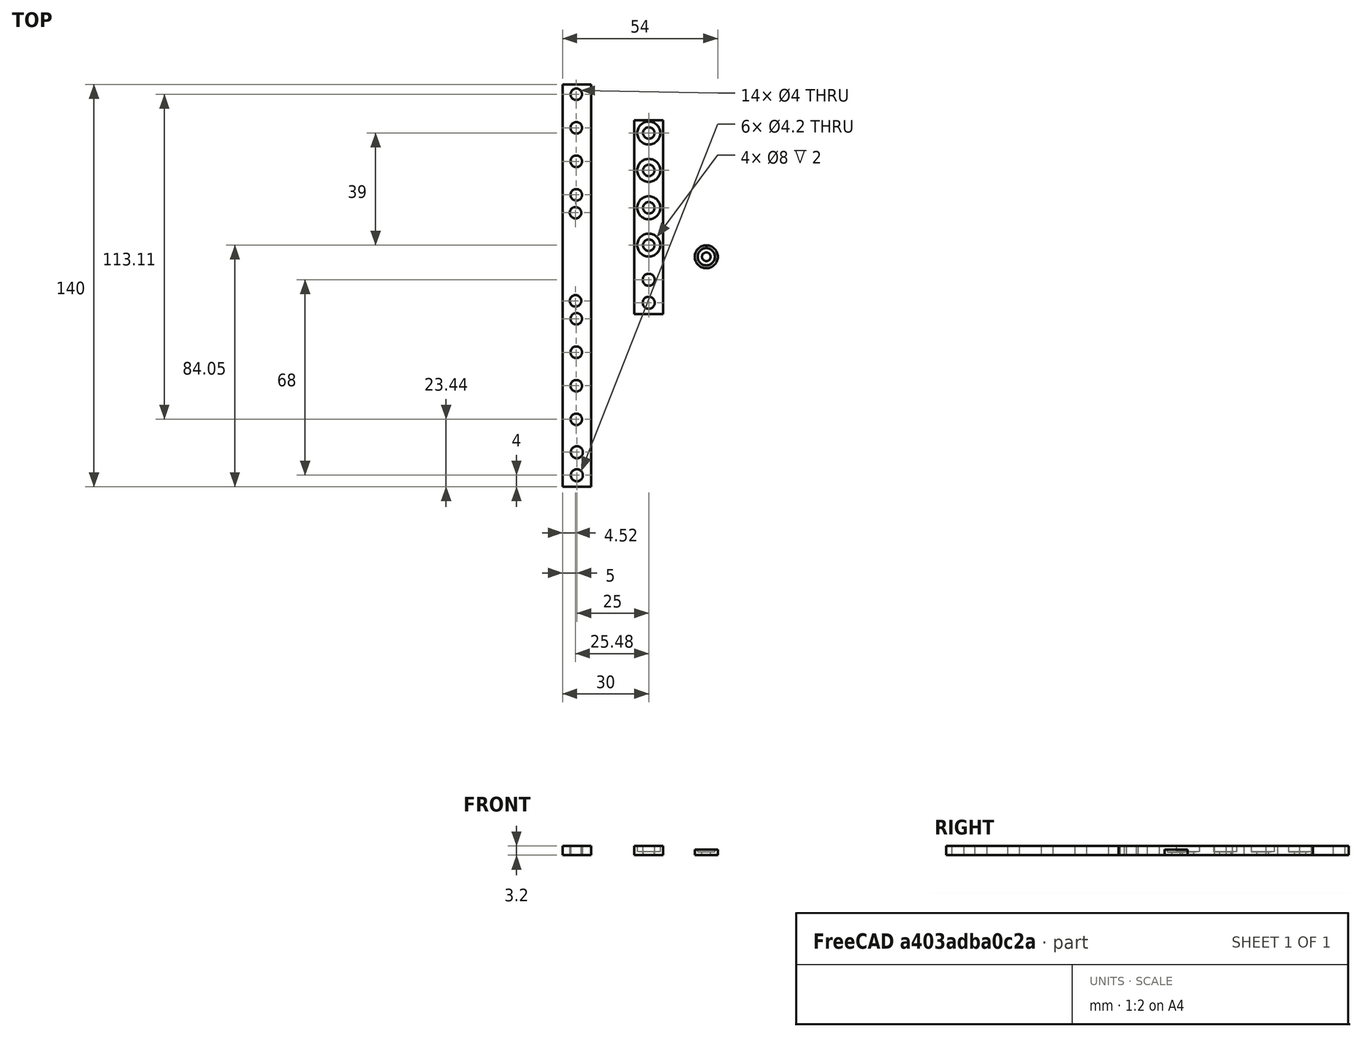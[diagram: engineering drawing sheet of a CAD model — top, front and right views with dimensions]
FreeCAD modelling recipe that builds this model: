
FCSTD DOCUMENT  (FreeCAD 0.19R24291 (Git))
Label: busbars
License: All rights reserved
LicenseURL: http://en.wikipedia.org/wiki/All_rights_reserved
objects: TechDraw::DrawViewDimension×44, Part::Cylinder×18, PartDesign::Line×18, Part::Fuse×7, TechDraw::DrawProjGroupItem×6, Part::Box×5, Part::Cut×5, Part::MultiFuse×4, Sketcher::SketchObject×3, PartDesign::CoordinateSystem×3, PartDesign::Hole×3, PartDesign::Body×3, Part::Part2DObjectPython×2, PartDesign::Pad×2, TechDraw::DrawProjGroup×2, App::DocumentObjectGroup×2, TechDraw::DrawViewPart×2, Part::FeaturePython×2, Part::Mirroring×1, TechDraw::DrawSVGTemplate×1, +4 more types
note: 82 computed .brp shape members not serialized (recipe doc carries the construction recipe); baked Part::Feature solids carry a one-line shape summary decoded from their .brp

FEATURE [Part::Box] cube
  AttacherType = Attacher::AttachEngine3D
  Height = 3
  Length = 10
  Width = 60
FEATURE [Part::Cylinder] cylinder
  Angle = 360
  AttacherType = Attacher::AttachEngine3D
  Height = 5
  Placement = pos=(4.81,56.54,-1) rot=(0,0,1;0rad)
  Radius = 1.6
FEATURE [Part::Cylinder] cylinder001
  Angle = 360
  AttacherType = Attacher::AttachEngine3D
  Height = 5
  Placement = pos=(4.81,44.87,-1) rot=(0,0,1;0rad)
  Radius = 1.6
FEATURE [Part::Cylinder] cylinder002
  Angle = 360
  AttacherType = Attacher::AttachEngine3D
  Height = 5
  Placement = pos=(4.81,33.2,-1) rot=(0,0,1;0rad)
  Radius = 1.6
FEATURE [Part::Cylinder] cylinder003
  Angle = 360
  AttacherType = Attacher::AttachEngine3D
  Height = 5
  Placement = pos=(4.81,21.53,-1) rot=(0,0,1;0rad)
  Radius = 1.6
FEATURE [Part::MultiFuse] Group
  Shapes = -> [cylinder,cylinder001,cylinder002,cylinder003]
FEATURE [Part::Cylinder] cylinder004
  Angle = 360
  AttacherType = Attacher::AttachEngine3D
  Height = 5
  Placement = pos=(4.52,15.3,-1) rot=(0,0,1;0rad)
  Radius = 1.6
FEATURE [Part::Fuse] union
  Base = -> Group
  Tool = -> cylinder004
FEATURE [Part::Cut] difference
  Base = -> cube
  Tool = -> union
FEATURE [Part::Box] cube001
  AttacherType = Attacher::AttachEngine3D
  Height = 3
  Length = 10
  Width = 60
FEATURE [Part::Cylinder] cylinder005 .. cylinder008  x4 (patterned run collapsed; names and placements below)
  Angle = 360
  AttacherType = Attacher::AttachEngine3D
  Height = 5
  Radius = 1.6
  placements: 4 in arithmetic series — first pos=(4.81,56.54,-1) rot=(0,0,1;0rad), step (0,-11.67,0), last pos=(4.81,21.53,-1) rot=(0,0,1;0rad)
FEATURE [Part::MultiFuse] Group001
  Shapes = -> [cylinder005,cylinder006,cylinder007,cylinder008]
FEATURE [Part::Cylinder] cylinder009
  Angle = 360
  AttacherType = Attacher::AttachEngine3D
  Height = 5
  Placement = pos=(4.52,15.3,-1) rot=(0,0,1;0rad)
  Radius = 1.6
FEATURE [Part::Fuse] union001
  Base = -> Group001
  Tool = -> cylinder009
FEATURE [Part::Cut] difference001
  Base = -> cube001
  Tool = -> union001
FEATURE [Part::Mirroring] mirr_difference001  label="mirrored difference001"
  Base = (0,0,0)
  Normal = (0,1,0)
  Source = -> difference001
FEATURE [Part::Fuse] Group002
  Base = -> difference
  Tool = -> mirr_difference001
FEATURE [Part::Box] cube002
  AttacherType = Attacher::AttachEngine3D
  Height = 3
  Length = 10
  Placement = pos=(0,-80,0) rot=(0,0,1;0rad)
  Width = 20
FEATURE [Part::Cylinder] cylinder010
  Angle = 360
  AttacherType = Attacher::AttachEngine3D
  Height = 5
  Placement = pos=(5,-76,-1) rot=(0,0,1;0rad)
  Radius = 2.1
FEATURE [Part::Cylinder] cylinder011
  Angle = 360
  AttacherType = Attacher::AttachEngine3D
  Height = 5
  Placement = pos=(5,-68,-1) rot=(0,0,1;0rad)
  Radius = 2.1
FEATURE [Part::Fuse] union002
  Base = -> cylinder010
  Tool = -> cylinder011
FEATURE [Part::Cut] difference002
  Base = -> cube002
  Tool = -> union002
FEATURE [Part::Fuse] union003  label="bar1_fromOpenScad"
  Base = -> Group002
  Tool = -> difference002
FEATURE [Part::Box] cube003
  AttacherType = Attacher::AttachEngine3D
  Height = 3
  Length = 10
  Width = 60
FEATURE [Part::Cylinder] cylinder012 .. cylinder015  x4 (patterned run collapsed; names and placements below)
  Angle = 360
  AttacherType = Attacher::AttachEngine3D
  Height = 5
  Radius = 1.6
  placements: 4 in arithmetic series — first pos=(5,8.86,-1) rot=(0,0,1;0rad), step (0,13.8925,0), last pos=(5,50.5375,-1) rot=(0,0,1;0rad)
FEATURE [Part::MultiFuse] Group003
  Shapes = -> [cylinder012,cylinder013,cylinder014,cylinder015]
FEATURE [Part::Cut] difference003
  Base = -> cube003
  Tool = -> Group003
FEATURE [Part::Box] cube004
  AttacherType = Attacher::AttachEngine3D
  Height = 3
  Length = 10
  Placement = pos=(0,-20,0) rot=(0,0,1;0rad)
  Width = 20
FEATURE [Part::Cylinder] cylinder016
  Angle = 360
  AttacherType = Attacher::AttachEngine3D
  Height = 5
  Placement = pos=(5,-16,-1) rot=(0,0,1;0rad)
  Radius = 2.1
FEATURE [Part::Cylinder] cylinder017
  Angle = 360
  AttacherType = Attacher::AttachEngine3D
  Height = 5
  Placement = pos=(5,-8,-1) rot=(0,0,1;0rad)
  Radius = 2.1
FEATURE [Part::Fuse] union004
  Base = -> cylinder016
  Tool = -> cylinder017
FEATURE [Part::Cut] difference004
  Base = -> cube004
  Tool = -> union004
FEATURE [Part::Fuse] union005  label="bar2_fromOpenScad"
  Base = -> difference003
  Placement = pos=(25,0,0) rot=(0,0,1;0rad)
  Tool = -> difference004
FEATURE [TechDraw::DrawSVGTemplate] Template
  EditableTexts = APPROVER_NAME=APPROVER NAME,AUTHOR_NAME=AUTHOR NAME,DATE=YYYY-MM-DD,DN=DN,DOCUMENT_TYPE=Mechanical assembly drawing,OWNER_NAME=OWNER NAME,PM=PM,PN=PN,+7 more (map truncated)
  Height = 297
  Orientation = 1
  Width = 420
FEATURE [Part::Part2DObjectPython] Shape2DView  label="bar1_Shape2DView"  # Draft 2D object (typed FeaturePython)
  Base = -> union003
  FuseArch = false
  HiddenLines = false
  InPlace = true
  Projection = (0,0,1)
  ProjectionMode = 0
  SegmentLength = 0.05
  Tessellation = false
  VisibleOnly = false
FEATURE [Sketcher::SketchObject] Sketch  label="bar1_Sketch"
  FullyConstrained = true
  expr: Constraints[47] = Spreadsheet.varH
  expr: Constraints[46] = 2 * Spreadsheet.tab / 5
  expr: Constraints[33] = Spreadsheet.varA
  expr: Constraints[20] = Spreadsheet.varD
  expr: Constraints[45] = Spreadsheet.tab / 5
  expr: Constraints[34] = Spreadsheet.varA
  expr: Constraints[36] = Spreadsheet.varC
  expr: Constraints[41] = Spreadsheet.varE
  expr: Constraints[40] = Spreadsheet.varE
  expr: Constraints[39] = Spreadsheet.varD
  expr: Constraints[37] = Spreadsheet.varC
  expr: Constraints[35] = Spreadsheet.varA
  expr: Constraints[31] = Spreadsheet.varA
  expr: Constraints[25] = Spreadsheet.lenght1
  expr: Constraints[28] = Spreadsheet.varC
  expr: Constraints[30] = Spreadsheet.varA
  expr: Constraints[8] = Spreadsheet.hole2_diameter
  expr: Constraints[44] = Spreadsheet.width / 2
  expr: Constraints[19] = Spreadsheet.varA
  expr: Constraints[42] = Spreadsheet.varB
  expr: Constraints[7] = Spreadsheet.hole2_diameter
  expr: Constraints[43] = Spreadsheet.width / 2
  expr: Constraints[27] = Spreadsheet.varC
  expr: Constraints[9] = Spreadsheet.hole1_diameter
  expr: Constraints[32] = Spreadsheet.varA
  expr: Constraints[26] = Spreadsheet.varC
  expr: Constraints[3] = Spreadsheet.width
  expr: Constraints[29] = Spreadsheet.varA
  expr: Constraints[38] = Spreadsheet.varC
  sketch-geometry (16):
    g0: LineSegment StartX=0 StartY=60 StartZ=0 EndX=10 EndY=60 EndZ=0
    g1: Circle CenterX=4.52 CenterY=15.32 CenterZ=0 NormalX=0 NormalY=0 NormalZ=1 AngleXU=0 Radius=2
    g2: Circle CenterX=4.81 CenterY=21.54 CenterZ=0 NormalX=0 NormalY=0 NormalZ=1 AngleXU=0 Radius=2
    g3: Circle CenterX=4.81 CenterY=33.21 CenterZ=0 NormalX=0 NormalY=0 NormalZ=1 AngleXU=0 Radius=2
    g4: Circle CenterX=4.81 CenterY=44.88 CenterZ=0 NormalX=0 NormalY=0 NormalZ=1 AngleXU=0 Radius=2
    g5: Circle CenterX=4.81 CenterY=56.55 CenterZ=0 NormalX=0 NormalY=0 NormalZ=1 AngleXU=0 Radius=2
    g6: Circle CenterX=4.52 CenterY=-15.33 CenterZ=0 NormalX=0 NormalY=0 NormalZ=-1 AngleXU=-3.14159 Radius=2
    g7: Circle CenterX=4.81 CenterY=-21.55 CenterZ=0 NormalX=0 NormalY=0 NormalZ=-1 AngleXU=-3.14159 Radius=2
    g8: Circle CenterX=4.81 CenterY=-33.22 CenterZ=0 NormalX=0 NormalY=0 NormalZ=-1 AngleXU=-3.14159 Radius=2
    g9: Circle CenterX=4.81 CenterY=-44.89 CenterZ=0 NormalX=0 NormalY=0 NormalZ=-1 AngleXU=-3.14159 Radius=2
    g10: Circle CenterX=4.81 CenterY=-56.56 CenterZ=0 NormalX=0 NormalY=0 NormalZ=-1 AngleXU=-3.14159 Radius=2
    g11: LineSegment StartX=0 StartY=-80 StartZ=0 EndX=10 EndY=-80 EndZ=0
    g12: Circle CenterX=5 CenterY=-76 CenterZ=0 NormalX=0 NormalY=0 NormalZ=1 AngleXU=0 Radius=2.1
    g13: Circle CenterX=5 CenterY=-68 CenterZ=0 NormalX=0 NormalY=0 NormalZ=1 AngleXU=0 Radius=2.1
    g14: LineSegment StartX=0 StartY=60 StartZ=0 EndX=0 EndY=-80 EndZ=0
    g15: LineSegment StartX=10 StartY=-80 StartZ=0 EndX=10 EndY=60 EndZ=0
  constraints (50):
    c: Horizontal(g11)
    c: Horizontal(g0)
    c: Vertical(g14)
    c: Distance(g11) = 10
    c: Coincident(g11,g14)
    c: DistanceX(g11) = 0
    c: DistanceY(g11) = -80
    c: Diameter(g12) = 4.2
    c: Diameter(g13) = 4.2
    c: Diameter(g10) = 4
    c: Equal(g5,g4)
    c: Equal(g4,g3)
    c: Equal(g3,g2)
    c: Equal(g2,g1)
    c: Equal(g1,g7)
    c: Equal(g7,g6)
    c: Equal(g6,g8)
    c: Equal(g8,g10)
    c: Equal(g9,g10)
    c: Distance(g9,g14) = 4.81
    c: Distance(g6,g14) = 4.52
    c: Vertical(g15)
    c: Coincident(g0,g14)
    c: Coincident(g0,g15)
    c: Coincident(g15,g11)
    c: DistanceY(g11,g0) = 140
    c: DistanceY(g10,g9) = 11.67
    c: DistanceY(g9,g8) = 11.67
    c: DistanceY(g8,g7) = 11.67
    c: Distance(g10,g14) = 4.81
    c: Distance(g8,g14) = 4.81
    c: Distance(g7,g14) = 4.81
    c: Distance(g2,g14) = 4.81
    c: Distance(g3,g14) = 4.81
    c: Distance(g4,g14) = 4.81
    c: Distance(g5,g14) = 4.81
    c: DistanceY(g2,g3) = 11.67
    c: DistanceY(g3,g4) = 11.67
    c: DistanceY(g4,g5) = 11.67
    c: Distance(g1,g14) = 4.52
    c: DistanceY(g7,g6) = 6.22
    c: DistanceY(g1,g2) = 6.22
    c: Distance(g5,g0) = 3.45
    c: Distance(g12,g14) = 5
    c: Distance(g13,g14) = 5
    c: Distance(g12,g11) = 4
    c: DistanceY(g12,g13) = 8
    c: DistanceY(g6,g1) = 30.65
    c: Distance(g10,g11) = 23.44
    c: DistanceY(g13,g10) = 11.44
FEATURE [Part::Part2DObjectPython] Shape2DView001  label="bar2_Shape2DView"  # Draft 2D object (typed FeaturePython)
  Base = -> union005
  FuseArch = false
  HiddenLines = false
  InPlace = true
  Projection = (0,0,1)
  ProjectionMode = 0
  SegmentLength = 0.05
  Tessellation = false
  VisibleOnly = false
FEATURE [Sketcher::SketchObject] Sketch001  label="bar2_Sketch"
  FullyConstrained = true
  expr: Constraints[29] = Spreadsheet.varG
  expr: Constraints[26] = Spreadsheet.width / 2
  expr: Constraints[24] = Spreadsheet.width / 2
  expr: Constraints[28] = Spreadsheet.varG
  expr: Constraints[25] = Spreadsheet.width / 2
  expr: Constraints[21] = Spreadsheet.hole1_diameter
  expr: Constraints[23] = Spreadsheet.width / 2
  expr: Constraints[19] = Spreadsheet.hole1_diameter
  expr: Constraints[18] = Spreadsheet.hole1_diameter
  expr: Constraints[20] = Spreadsheet.hole1_diameter
  expr: Constraints[15] = Spreadsheet.width / 2
  expr: Constraints[13] = 2 * Spreadsheet.tab / 5
  expr: Constraints[12] = Spreadsheet.tab / 5
  expr: Constraints[22] = Spreadsheet.varF
  expr: Constraints[14] = Spreadsheet.width / 2
  expr: Constraints[17] = Spreadsheet.hole2_diameter
  expr: Constraints[9] = Spreadsheet.length2
  expr: Constraints[27] = Spreadsheet.varG
  expr: Constraints[16] = Spreadsheet.hole2_diameter
  expr: Constraints[8] = Spreadsheet.width
  sketch-geometry (10):
    g0: LineSegment StartX=25 StartY=47.5 StartZ=0 EndX=35 EndY=47.5 EndZ=0
    g1: Circle CenterX=30 CenterY=4.05 CenterZ=0 NormalX=0 NormalY=0 NormalZ=1 AngleXU=0 Radius=2
    g2: Circle CenterX=30 CenterY=17.05 CenterZ=0 NormalX=0 NormalY=0 NormalZ=1 AngleXU=0 Radius=2
    g3: Circle CenterX=30 CenterY=30.05 CenterZ=0 NormalX=0 NormalY=0 NormalZ=1 AngleXU=0 Radius=2
    g4: Circle CenterX=30 CenterY=43.05 CenterZ=0 NormalX=0 NormalY=0 NormalZ=1 AngleXU=0 Radius=2
    g5: LineSegment StartX=25 StartY=-20 StartZ=0 EndX=35 EndY=-20 EndZ=0
    g6: Circle CenterX=30 CenterY=-16 CenterZ=0 NormalX=0 NormalY=0 NormalZ=1 AngleXU=0 Radius=2.1
    g7: Circle CenterX=30 CenterY=-8 CenterZ=0 NormalX=0 NormalY=0 NormalZ=1 AngleXU=0 Radius=2.1
    g8: LineSegment StartX=35 StartY=-20 StartZ=0 EndX=35 EndY=47.5 EndZ=0
    g9: LineSegment StartX=25 StartY=47.5 StartZ=0 EndX=25 EndY=-20 EndZ=0
  constraints (32):
    c: Coincident(g8,g0)
    c: Coincident(g0,g9)
    c: Coincident(g9,g5)
    c: Coincident(g5,g8)
    c: Vertical(g8)
    c: Vertical(g9)
    c: Horizontal(g5)
    c: Horizontal(g0)
    c: Distance(g5) = 10
    c: Distance(g9) = 67.5
    c: DistanceX(g5) = 25
    c: DistanceY(g5) = -20
    c: Distance(g6,g5) = 4
    c: DistanceY(g6,g7) = 8
    c: Distance(g7,g9) = 5
    c: Distance(g6,g9) = 5
    c: Diameter(g7) = 4.2
    c: Diameter(g6) = 4.2
    c: Diameter(g1) = 4
    c: Diameter(g2) = 4
    c: Diameter(g3) = 4
    c: Diameter(g4) = 4
    c: Distance(g4,g0) = 4.45
    c: Distance(g1,g9) = 5
    c: Distance(g2,g9) = 5
    c: Distance(g4,g9) = 5
    c: Distance(g3,g9) = 5
    c: Distance(g4,g3) = 13
    c: Distance(g3,g2) = 13
    c: Distance(g1,g2) = 13
    c: Distance(g1,g5) = 24.05
    c: Distance(g7,g1) = 12.05
FEATURE [Spreadsheet::Sheet] Spreadsheet  label="Dimensions"
  cells = A1=Parameter; B1=Value; C1=Description; A2=L1; B2(lenght1)==120mm + tab; C2=Comprimento da barra 1; A3=L2; B3(length2)==50mm + tab - 2.5mm; C3=Comprimento da barra 2; A4=W; B4(width)==10mm; C4=Largura das barras; A5=T; B5(thickness)==3.2mm; C5=Espessura das barras; A6=H1; B6(hole1_diameter)==4mm; C6=Diâmetro interno do furo sem rosca; A7=H2; B7(hole2_diameter)==4.2mm; C7=Furo com rosca M5; A8=A; B8(varA)==4.81mm; C8=Distância entre a borda lateral da barra e centro do furo; A9=B; B9(varB)==3.45mm; A10=C; B10(varC)==11.67mm; A11=D; B11(varD)==4.52mm; C11=Distância entre a borda lateral da barra e centro do furo; A12=E; B12(varE)==6.22mm; A13=F; B13(varF)==4.45mm; C13=Distância entre a borda frontal da barra e centro do furo; A14=G; B14(varG)==13mm; A15=H; B15(varH)==30.65mm; A16=Tab; B16(tab)==20mm
FEATURE [PartDesign::Pad] Pad  label="bar1_Pad"
  Direction = (1,1,1)
  Length = 3.2
  Length2 = 100
  Profile = -> Sketch
  Type = 0
  expr: Length = Spreadsheet.thickness
FEATURE [PartDesign::Pad] Pad001  label="bar2_Pad"
  Direction = (1,1,1)
  Length = 3.2
  Length2 = 100
  Profile = -> Sketch001
  Type = 0
  expr: Length = Spreadsheet.thickness
FEATURE [TechDraw::DrawViewSpreadsheet] Sheet
  CellEnd = B15
  CellStart = A1
  Font = osifont
  LineWidth = 0.35
  LockPosition = false
  Rotation = 0
  ScaleType = 2
  Source = -> Spreadsheet
  Symbol = <blob: 6326 chars omitted>
  TextSize = 12
  X = 376.234
  Y = 116.135
FEATURE [PartDesign::CoordinateSystem] LCS_1
  AttacherType = Attacher::AttachEngine3D
  MapMode = 6
  Placement = pos=(10,60,3.2) rot=(0,0,1;3.14159rad)
  Support = -> [Pad]
FEATURE [PartDesign::CoordinateSystem] LCS_2
  AttacherType = Attacher::AttachEngine3D
  MapMode = 6
  Placement = pos=(35,47.5,3.2) rot=(0,0,1;3.14159rad)
  Support = -> [Pad001]
FEATURE [PartDesign::Line] HoleAxis_1
  AttacherType = Attacher::AttachEngineLine
  Length = 5.91808
  MapMode = 19
  Placement = pos=(30,-8,3.2) rot=(0,0,1;0rad)
  ResizeMode = 1
  Support = -> [Pad001]
FEATURE [PartDesign::Line] HoleAxis_2
  AttacherType = Attacher::AttachEngineLine
  Length = 5.91808
  MapMode = 19
  Placement = pos=(30,-16,3.2) rot=(0,0,1;0rad)
  ResizeMode = 1
  Support = -> [Pad001]
FEATURE [PartDesign::Line] HoleAxis_3
  AttacherType = Attacher::AttachEngineLine
  Length = 5.63627
  MapMode = 19
  Placement = pos=(30,17.05,3.2) rot=(0,0,1;0rad)
  ResizeMode = 1
  Support = -> [Pad001]
FEATURE [PartDesign::Line] HoleAxis_4
  AttacherType = Attacher::AttachEngineLine
  Length = 5.63627
  MapMode = 19
  Placement = pos=(30,30.05,3.2) rot=(0,0,1;0rad)
  ResizeMode = 1
  Support = -> [Pad001]
FEATURE [PartDesign::Line] HoleAxis_5
  AttacherType = Attacher::AttachEngineLine
  Length = 5.63627
  MapMode = 19
  Placement = pos=(30,4.05,3.2) rot=(0,0,1;0rad)
  ResizeMode = 1
  Support = -> [Pad001]
FEATURE [PartDesign::Line] HoleAxis_6
  AttacherType = Attacher::AttachEngineLine
  Length = 5.63627
  MapMode = 19
  Placement = pos=(30,43.05,3.2) rot=(0,0,1;0rad)
  ResizeMode = 1
  Support = -> [Pad001]
FEATURE [PartDesign::Line] HoleAxis_7
  AttacherType = Attacher::AttachEngineLine
  Length = 5.63627
  MapMode = 19
  Placement = pos=(4.81,56.55,3.2) rot=(0,0,1;0rad)
  ResizeMode = 1
  Support = -> [Pad]
FEATURE [PartDesign::Line] HoleAxis_8
  AttacherType = Attacher::AttachEngineLine
  Length = 5.63627
  MapMode = 19
  Placement = pos=(4.81,44.88,3.2) rot=(0,0,1;0rad)
  ResizeMode = 1
  Support = -> [Pad]
FEATURE [PartDesign::Line] HoleAxis_9
  AttacherType = Attacher::AttachEngineLine
  Length = 5.63627
  MapMode = 19
  Placement = pos=(4.81,33.21,3.2) rot=(0,0,1;0rad)
  ResizeMode = 1
  Support = -> [Pad]
FEATURE [PartDesign::Line] HoleAxis_10
  AttacherType = Attacher::AttachEngineLine
  Length = 5.63627
  MapMode = 19
  Placement = pos=(4.52,15.32,3.2) rot=(0,0,1;0rad)
  ResizeMode = 1
  Support = -> [Pad]
FEATURE [PartDesign::Line] HoleAxis_11
  AttacherType = Attacher::AttachEngineLine
  Length = 5.63627
  MapMode = 19
  Placement = pos=(4.81,-33.22,3.2) rot=(-1,0,0;3.14159rad)
  ResizeMode = 1
  Support = -> [Pad]
FEATURE [PartDesign::Line] HoleAxis_12
  AttacherType = Attacher::AttachEngineLine
  Length = 5.63627
  MapMode = 19
  Placement = pos=(4.81,21.54,3.2) rot=(0,0,1;0rad)
  ResizeMode = 1
  Support = -> [Pad]
FEATURE [PartDesign::Line] HoleAxis_13
  AttacherType = Attacher::AttachEngineLine
  Length = 5.63627
  MapMode = 19
  Placement = pos=(4.81,-21.55,3.2) rot=(-1,0,0;3.14159rad)
  ResizeMode = 1
  Support = -> [Pad]
FEATURE [PartDesign::Line] HoleAxis_14
  AttacherType = Attacher::AttachEngineLine
  Length = 5.63627
  MapMode = 19
  Placement = pos=(4.52,-15.33,3.2) rot=(-1,0,0;3.14159rad)
  ResizeMode = 1
  Support = -> [Pad]
FEATURE [PartDesign::Line] HoleAxis_15
  AttacherType = Attacher::AttachEngineLine
  Length = 5.63627
  MapMode = 19
  Placement = pos=(4.81,-44.89,3.2) rot=(-1,0,0;3.14159rad)
  ResizeMode = 1
  Support = -> [Pad]
FEATURE [PartDesign::Line] HoleAxis_16
  AttacherType = Attacher::AttachEngineLine
  Length = 5.63627
  MapMode = 19
  Placement = pos=(4.81,-56.56,3.2) rot=(-1,0,0;3.14159rad)
  ResizeMode = 1
  Support = -> [Pad]
FEATURE [PartDesign::Line] HoleAxis_17
  AttacherType = Attacher::AttachEngineLine
  Length = 5.91808
  MapMode = 19
  Placement = pos=(5,-68,3.2) rot=(0,0,1;0rad)
  ResizeMode = 1
  Support = -> [Pad]
FEATURE [PartDesign::Line] HoleAxis_18
  AttacherType = Attacher::AttachEngineLine
  Length = 5.91808
  MapMode = 19
  Placement = pos=(5,-76,3.2) rot=(0,0,1;0rad)
  ResizeMode = 1
  Support = -> [Pad]
FEATURE [Sketcher::SketchObject] Sketch002
  FullyConstrained = true
  MapMode = 5
  Placement = pos=(0,0,3.2) rot=(0,0,1;0rad)
  Support = -> [Pad]
FEATURE [PartDesign::Hole] Hole
  BaseFeature = -> Pad001
  Depth = 25
  DepthType = 0
  Diameter = 3.4
  DrillForDepth = true
  DrillPoint = 1
  DrillPointAngle = 118
  HoleCutCountersinkAngle = 90
  HoleCutCustomValues = false
  HoleCutDepth = 2
  HoleCutDiameter = 8
  HoleCutType = 1
  ModelActualThread = false
  Profile = -> Pad001 [Edge30,Edge27,Edge21,Edge24]
  Tapered = false
  TaperedAngle = 90
  ThreadAngle = 0
  ThreadClass = 0
  ThreadCutOffInner = 0
  ThreadCutOffOuter = 0
  ThreadDirection = 0
  ThreadFit = 0
  ThreadPitch = 0
  ThreadSize = 9
  ThreadType = 1
  Threaded = false
FEATURE [PartDesign::Hole] Hole001
  BaseFeature = -> Hole
  Depth = 3
  DepthType = 0
  Diameter = 4.2
  DrillForDepth = false
  DrillPoint = 1
  DrillPointAngle = 118
  HoleCutCountersinkAngle = 90
  HoleCutCustomValues = false
  HoleCutDepth = 5.4
  HoleCutDiameter = 6.72
  HoleCutType = 0
  ModelActualThread = false
  Profile = -> Hole [Edge20,Edge19]
  Tapered = false
  TaperedAngle = 90
  ThreadAngle = 60
  ThreadClass = 0
  ThreadCutOffInner = 0.0866025
  ThreadCutOffOuter = 0.173205
  ThreadDirection = 0
  ThreadFit = 0
  ThreadPitch = 0.8
  ThreadSize = 13
  ThreadType = 1
  Threaded = true
FEATURE [PartDesign::Body] Body001  label="bar2_body"
  Group = -> [Sketch001,Pad001,LCS_2,HoleAxis_1,HoleAxis_2,HoleAxis_3,HoleAxis_4,HoleAxis_5,HoleAxis_6,Hole,Hole001]
  Origin = -> Origin001
  Tip = -> Hole001
FEATURE [TechDraw::DrawProjGroupItem] ProjItem003  label="Front001"
  CoarseView = false
  Direction = (0,0,1)
  Focus = 100
  HardHidden = false
  IsoCount = 0
  IsoHidden = false
  IsoVisible = false
  LockPosition = true
  Perspective = false
  Rotation = 0
  RotationVector = (1,0,0)
  ScaleType = 2
  SeamHidden = false
  SeamVisible = true
  SmoothHidden = false
  SmoothVisible = true
  Source = -> [Body001]
  Type = 0
  X = 0
  XDirection = (1,0,0)
  Y = 0
FEATURE [TechDraw::DrawProjGroupItem] ProjItem004  label="Bottom001"
  CoarseView = false
  Direction = (0,-1,0)
  Focus = 100
  HardHidden = false
  IsoCount = 0
  IsoHidden = false
  IsoVisible = false
  LockPosition = false
  Perspective = false
  Rotation = 0
  RotationVector = (1,0,0)
  ScaleType = 2
  SeamHidden = false
  SeamVisible = true
  SmoothHidden = false
  SmoothVisible = true
  Source = -> [Body001]
  Type = 5
  X = 0
  XDirection = (1,0,0)
  Y = 50.35
FEATURE [TechDraw::DrawProjGroupItem] ProjItem005  label="Right001"
  CoarseView = false
  Direction = (1,0,1e-16)
  Focus = 100
  HardHidden = false
  IsoCount = 0
  IsoHidden = false
  IsoVisible = false
  LockPosition = false
  Perspective = false
  Rotation = 0
  RotationVector = (1,0,0)
  ScaleType = 2
  SeamHidden = false
  SeamVisible = true
  SmoothHidden = false
  SmoothVisible = true
  Source = -> [Body001]
  Type = 2
  X = -21.6
  XDirection = (1e-16,0,-1)
  Y = 0
FEATURE [TechDraw::DrawProjGroup] ProjGroup001  label="bar2_ProjGroup"
  Anchor = -> ProjItem003
  AutoDistribute = true
  LockPosition = false
  ProjectionType = 0
  Rotation = 0
  ScaleType = 0
  Source = -> [Body001]
  Views = -> [ProjItem003,ProjItem004,ProjItem005]
  X = 229.028
  Y = 134.779
  spacingX = 15
  spacingY = 15
FEATURE [App::DocumentObjectGroup] Group005  label="bar2_group"
  Group = -> [union005,Shape2DView001,Body001,ProjGroup001]
FEATURE [TechDraw::DrawViewDimension] Dimension024
  Arbitrary = false
  ArbitraryTolerances = false
  EqualTolerance = true
  FormatSpec = %.2f
  FormatSpecOverTolerance = %+.2f
  FormatSpecUnderTolerance = %+.2f
  Inverted = false
  LockPosition = false
  MeasureType = 1
  OverTolerance = 0
  References2D = -> [ProjItem003]
  Rotation = 0
  ScaleType = 0
  TheoreticalExact = false
  Type = 2
  UnderTolerance = 0
  X = 13.4217
  Y = 0.123273
FEATURE [TechDraw::DrawViewDimension] Dimension025
  Arbitrary = false
  ArbitraryTolerances = false
  EqualTolerance = true
  FormatSpec = %.2f
  FormatSpecOverTolerance = %+.2f
  FormatSpecUnderTolerance = %+.2f
  Inverted = false
  LockPosition = false
  MeasureType = 1
  OverTolerance = 0
  References2D = -> [ProjItem003]
  Rotation = 0
  ScaleType = 0
  TheoreticalExact = false
  Type = 2
  UnderTolerance = 0
  X = 13.3126
  Y = 13.6689
FEATURE [TechDraw::DrawViewDimension] Dimension026
  Arbitrary = false
  ArbitraryTolerances = false
  EqualTolerance = true
  FormatSpec = %.2f
  FormatSpecOverTolerance = %+.2f
  FormatSpecUnderTolerance = %+.2f
  Inverted = false
  LockPosition = false
  MeasureType = 1
  OverTolerance = 0
  References2D = -> [ProjItem003]
  Rotation = 0
  ScaleType = 0
  TheoreticalExact = false
  Type = 2
  UnderTolerance = 0
  X = 13.3126
  Y = 26.2324
FEATURE [TechDraw::DrawViewDimension] Dimension027
  Arbitrary = false
  ArbitraryTolerances = false
  EqualTolerance = true
  FormatSpec = %.2f
  FormatSpecOverTolerance = %+.2f
  FormatSpecUnderTolerance = %+.2f
  Inverted = false
  LockPosition = false
  MeasureType = 1
  OverTolerance = 0
  References2D = -> [ProjItem003]
  Rotation = 0
  ScaleType = 0
  TheoreticalExact = false
  Type = 2
  UnderTolerance = 0
  X = 13.4217
  Y = -13.6517
FEATURE [TechDraw::DrawViewDimension] Dimension028
  Arbitrary = false
  ArbitraryTolerances = false
  EqualTolerance = true
  FormatSpec = %.2f
  FormatSpecOverTolerance = %+.2f
  FormatSpecUnderTolerance = %+.2f
  Inverted = false
  LockPosition = false
  MeasureType = 1
  OverTolerance = 0
  References2D = -> [ProjItem003]
  Rotation = 0
  ScaleType = 0
  TheoreticalExact = false
  Type = 2
  UnderTolerance = 0
  X = 29.0448
  Y = -15.0874
FEATURE [TechDraw::DrawViewDimension] Dimension029
  Arbitrary = false
  ArbitraryTolerances = false
  EqualTolerance = true
  FormatSpec = %.2f
  FormatSpecOverTolerance = %+.2f
  FormatSpecUnderTolerance = %+.2f
  Inverted = false
  LockPosition = false
  MeasureType = 1
  OverTolerance = 0
  References2D = -> [ProjItem003]
  Rotation = 0
  ScaleType = 0
  TheoreticalExact = false
  Type = 2
  UnderTolerance = 0
  X = 28.9947
  Y = 42.3775
FEATURE [TechDraw::DrawViewDimension] Dimension030
  Arbitrary = false
  ArbitraryTolerances = false
  EqualTolerance = true
  FormatSpec = %.2f
  FormatSpecOverTolerance = %+.2f
  FormatSpecUnderTolerance = %+.2f
  Inverted = false
  LockPosition = false
  MeasureType = 1
  OverTolerance = 0
  References2D = -> [ProjItem003]
  Rotation = 0
  ScaleType = 0
  TheoreticalExact = false
  Type = 2
  UnderTolerance = 0
  X = 20.9139
  Y = -38.0316
FEATURE [TechDraw::DrawViewDimension] Dimension031
  Arbitrary = false
  ArbitraryTolerances = false
  EqualTolerance = true
  FormatSpec = %.2f
  FormatSpecOverTolerance = %+.2f
  FormatSpecUnderTolerance = %+.2f
  Inverted = false
  LockPosition = false
  MeasureType = 1
  OverTolerance = 0
  References2D = -> [ProjItem003]
  Rotation = 0
  ScaleType = 0
  TheoreticalExact = false
  Type = 1
  UnderTolerance = 0
  X = -18.1472
  Y = -12.4166
FEATURE [TechDraw::DrawViewDimension] Dimension032
  Arbitrary = false
  ArbitraryTolerances = false
  EqualTolerance = true
  FormatSpec = ⌀%.2f
  FormatSpecOverTolerance = %+.2f
  FormatSpecUnderTolerance = %+.2f
  Inverted = false
  LockPosition = false
  MeasureType = 1
  OverTolerance = 0
  References2D = -> [ProjItem003]
  Rotation = 0
  ScaleType = 0
  TheoreticalExact = false
  Type = 5
  UnderTolerance = 0
  X = -19.2094
  Y = 8.43112
FEATURE [TechDraw::DrawViewDimension] Dimension033
  Arbitrary = true
  ArbitraryTolerances = false
  EqualTolerance = true
  FormatSpec = ⌀M5 c/ rosca
  FormatSpecOverTolerance = %+.2f
  FormatSpecUnderTolerance = %+.2f
  Inverted = false
  LockPosition = false
  MeasureType = 1
  OverTolerance = 0
  References2D = -> [ProjItem003]
  Rotation = 0
  ScaleType = 0
  TheoreticalExact = false
  Type = 5
  UnderTolerance = 0
  X = -22.7419
  Y = -33.2918
FEATURE [TechDraw::DrawViewDimension] Dimension035
  Arbitrary = true
  ArbitraryTolerances = false
  EqualTolerance = true
  FormatSpec = ⌀M5 c/ rosca
  FormatSpecOverTolerance = %+.2f
  FormatSpecUnderTolerance = %+.2f
  Inverted = false
  LockPosition = false
  MeasureType = 1
  OverTolerance = 0
  References2D = -> [ProjItem003]
  Rotation = 0
  ScaleType = 0
  TheoreticalExact = false
  Type = 5
  UnderTolerance = 0
  X = -23.8113
  Y = -25.5326
FEATURE [TechDraw::DrawViewDimension] Dimension043
  Arbitrary = false
  ArbitraryTolerances = false
  EqualTolerance = true
  FormatSpec = %.2f
  FormatSpecOverTolerance = %+.2f
  FormatSpecUnderTolerance = %+.2f
  Inverted = false
  LockPosition = false
  MeasureType = 1
  OverTolerance = 0
  References2D = -> [ProjItem005]
  Rotation = 0
  ScaleType = 0
  TheoreticalExact = false
  Type = 2
  UnderTolerance = 0
  X = -14.6369
  Y = 1.23933
FEATURE [TechDraw::DrawViewDimension] Dimension044
  Arbitrary = false
  ArbitraryTolerances = false
  EqualTolerance = true
  FormatSpec = %.2f
  FormatSpecOverTolerance = %+.2f
  FormatSpecUnderTolerance = %+.2f
  Inverted = false
  LockPosition = false
  MeasureType = 1
  OverTolerance = 0
  References2D = -> [ProjItem005]
  Rotation = 0
  ScaleType = 0
  TheoreticalExact = false
  Type = 1
  UnderTolerance = 0
  X = -0.495734
  Y = 44.6668
FEATURE [TechDraw::DrawViewDimension] Dimension045
  Arbitrary = false
  ArbitraryTolerances = false
  EqualTolerance = true
  FormatSpec = %.2f
  FormatSpecOverTolerance = %+.2f
  FormatSpecUnderTolerance = %+.2f
  Inverted = false
  LockPosition = false
  MeasureType = 1
  OverTolerance = 0
  References2D = -> [ProjItem004]
  Rotation = 0
  ScaleType = 0
  TheoreticalExact = false
  Type = 1
  UnderTolerance = 0
  X = 0
  Y = 13.6455
FEATURE [TechDraw::DrawViewPart] View001
  CoarseView = false
  Direction = (0.577,-0.577,0.577)
  Focus = 100
  HardHidden = false
  IsoCount = 0
  IsoHidden = false
  IsoVisible = false
  LockPosition = false
  Perspective = false
  Rotation = 0
  ScaleType = 0
  SeamHidden = false
  SeamVisible = true
  SmoothHidden = false
  SmoothVisible = true
  Source = -> [Body001]
  X = 212.253
  XDirection = (0.707,0.707,0)
  Y = 231.311
FEATURE [PartDesign::Hole] Hole002
  BaseFeature = -> Pad
  Depth = 25
  DepthType = 0
  Diameter = 4.2
  DrillForDepth = false
  DrillPoint = 1
  DrillPointAngle = 118
  HoleCutCountersinkAngle = 90
  HoleCutCustomValues = false
  HoleCutDepth = 0
  HoleCutDiameter = 6.1
  HoleCutType = 0
  ModelActualThread = false
  Profile = -> Pad [Edge15,Edge18]
  Tapered = false
  TaperedAngle = 90
  ThreadAngle = 60
  ThreadClass = 0
  ThreadCutOffInner = 0.0866025
  ThreadCutOffOuter = 0.173205
  ThreadDirection = 0
  ThreadFit = 0
  ThreadPitch = 0.8
  ThreadSize = 13
  ThreadType = 1
  Threaded = true
FEATURE [PartDesign::Body] Body  label="bar1_Body"
  Group = -> [Sketch,Pad,LCS_1,HoleAxis_7,HoleAxis_8,HoleAxis_9,HoleAxis_10,HoleAxis_11,HoleAxis_12,HoleAxis_13,HoleAxis_14,HoleAxis_15,HoleAxis_16,HoleAxis_17,HoleAxis_18,Hole002]
  Origin = -> Origin
  Tip = -> Hole002
FEATURE [TechDraw::DrawProjGroupItem] ProjItem  label="Front"
  CoarseView = false
  Direction = (0,0,1)
  Focus = 100
  HardHidden = false
  IsoCount = 0
  IsoHidden = false
  IsoVisible = false
  LockPosition = true
  Perspective = false
  Rotation = 0
  RotationVector = (1,0,0)
  ScaleType = 2
  SeamHidden = false
  SeamVisible = true
  SmoothHidden = false
  SmoothVisible = true
  Source = -> [Body]
  Type = 0
  X = 0
  XDirection = (1,0,0)
  Y = 0
FEATURE [TechDraw::DrawProjGroupItem] ProjItem001  label="Right"
  CoarseView = false
  Direction = (1,0,1e-16)
  Focus = 100
  HardHidden = false
  IsoCount = 0
  IsoHidden = false
  IsoVisible = false
  LockPosition = false
  Perspective = false
  Rotation = 0
  RotationVector = (1,0,0)
  ScaleType = 2
  SeamHidden = false
  SeamVisible = true
  SmoothHidden = false
  SmoothVisible = true
  Source = -> [Body]
  Type = 2
  X = -21.6
  XDirection = (1e-16,0,-1)
  Y = 0
FEATURE [TechDraw::DrawProjGroupItem] ProjItem002  label="Bottom"
  CoarseView = false
  Direction = (0,-1,0)
  Focus = 100
  HardHidden = false
  IsoCount = 0
  IsoHidden = false
  IsoVisible = false
  LockPosition = false
  Perspective = false
  Rotation = 0
  RotationVector = (1,0,0)
  ScaleType = 2
  SeamHidden = false
  SeamVisible = true
  SmoothHidden = false
  SmoothVisible = true
  Source = -> [Body]
  Type = 5
  X = 0
  XDirection = (1,0,0)
  Y = 86.6
FEATURE [TechDraw::DrawProjGroup] ProjGroup  label="bar1_ProjGroup"
  Anchor = -> ProjItem
  AutoDistribute = true
  LockPosition = false
  ProjectionType = 0
  Rotation = 0
  ScaleType = 0
  Source = -> [Body]
  Views = -> [ProjItem,ProjItem001,ProjItem002]
  X = 113.787
  Y = 98.3052
  spacingX = 15
  spacingY = 15
FEATURE [App::DocumentObjectGroup] Group004  label="bar1_group"
  Group = -> [union003,Shape2DView,Body,ProjGroup]
FEATURE [TechDraw::DrawViewDimension] Dimension001
  Arbitrary = false
  ArbitraryTolerances = false
  EqualTolerance = true
  FormatSpec = %.2f
  FormatSpecOverTolerance = %+.2f
  FormatSpecUnderTolerance = %+.2f
  Inverted = false
  LockPosition = false
  MeasureType = 1
  OverTolerance = 0
  References2D = -> [ProjItem]
  Rotation = 0
  ScaleType = 0
  TheoreticalExact = false
  Type = 1
  UnderTolerance = 0
  X = -17.6797
  Y = -35.607
FEATURE [TechDraw::DrawViewDimension] Dimension
  Arbitrary = false
  ArbitraryTolerances = false
  EqualTolerance = true
  FormatSpec = %.2f
  FormatSpecOverTolerance = %+.2f
  FormatSpecUnderTolerance = %+.2f
  Inverted = false
  LockPosition = false
  MeasureType = 1
  OverTolerance = 0
  References2D = -> [ProjItem]
  Rotation = 0
  ScaleType = 0
  TheoreticalExact = false
  Type = 1
  UnderTolerance = 0
  X = -17.4484
  Y = -47.7836
FEATURE [TechDraw::DrawViewDimension] Dimension003
  Arbitrary = false
  ArbitraryTolerances = false
  EqualTolerance = true
  FormatSpec = %.2f
  FormatSpecOverTolerance = %+.2f
  FormatSpecUnderTolerance = %+.2f
  Inverted = false
  LockPosition = false
  MeasureType = 1
  OverTolerance = 0
  References2D = -> [ProjItem]
  Rotation = 0
  ScaleType = 0
  TheoreticalExact = false
  Type = 2
  UnderTolerance = 0
  X = 13.8288
  Y = -38.2243
FEATURE [TechDraw::DrawViewDimension] Dimension004
  Arbitrary = false
  ArbitraryTolerances = false
  EqualTolerance = true
  FormatSpec = %.2f
  FormatSpecOverTolerance = %+.2f
  FormatSpecUnderTolerance = %+.2f
  Inverted = false
  LockPosition = false
  MeasureType = 1
  OverTolerance = 0
  References2D = -> [ProjItem]
  Rotation = 0
  ScaleType = 0
  TheoreticalExact = false
  Type = 2
  UnderTolerance = 0
  X = 13.8387
  Y = -26.3987
FEATURE [TechDraw::DrawViewDimension] Dimension005
  Arbitrary = false
  ArbitraryTolerances = false
  EqualTolerance = true
  FormatSpec = %.2f
  FormatSpecOverTolerance = %+.2f
  FormatSpecUnderTolerance = %+.2f
  Inverted = false
  LockPosition = false
  MeasureType = 1
  OverTolerance = 0
  References2D = -> [ProjItem]
  Rotation = 0
  ScaleType = 0
  TheoreticalExact = false
  Type = 2
  UnderTolerance = 0
  X = 13.8387
  Y = -15.1437
FEATURE [TechDraw::DrawViewDimension] Dimension006
  Arbitrary = false
  ArbitraryTolerances = false
  EqualTolerance = true
  FormatSpec = %.2f
  FormatSpecOverTolerance = %+.2f
  FormatSpecUnderTolerance = %+.2f
  Inverted = false
  LockPosition = false
  MeasureType = 1
  OverTolerance = 0
  References2D = -> [ProjItem]
  Rotation = 0
  ScaleType = 0
  TheoreticalExact = false
  Type = 2
  UnderTolerance = 0
  X = 20.2765
  Y = 1.03219
FEATURE [TechDraw::DrawViewDimension] Dimension007
  Arbitrary = false
  ArbitraryTolerances = false
  EqualTolerance = true
  FormatSpec = %.2f
  FormatSpecOverTolerance = %+.2f
  FormatSpecUnderTolerance = %+.2f
  Inverted = false
  LockPosition = false
  MeasureType = 1
  OverTolerance = 0
  References2D = -> [ProjItem]
  Rotation = 0
  ScaleType = 0
  TheoreticalExact = false
  Type = 2
  UnderTolerance = 0
  X = 28.4399
  Y = -50.4693
FEATURE [TechDraw::DrawViewDimension] Dimension008
  Arbitrary = false
  ArbitraryTolerances = false
  EqualTolerance = true
  FormatSpec = %.2f
  FormatSpecOverTolerance = %+.2f
  FormatSpecUnderTolerance = %+.2f
  Inverted = false
  LockPosition = false
  MeasureType = 1
  OverTolerance = 0
  References2D = -> [ProjItem]
  Rotation = 0
  ScaleType = 0
  TheoreticalExact = false
  Type = 2
  UnderTolerance = 0
  X = 19.8657
  Y = -73.109
FEATURE [TechDraw::DrawViewDimension] Dimension009
  Arbitrary = true
  ArbitraryTolerances = false
  EqualTolerance = true
  FormatSpec = ⌀M5 c/ rosca
  FormatSpecOverTolerance = %+.2f
  FormatSpecUnderTolerance = %+.2f
  Inverted = false
  LockPosition = false
  MeasureType = 1
  OverTolerance = 0
  References2D = -> [ProjItem]
  Rotation = 0
  ScaleType = 0
  TheoreticalExact = false
  Type = 5
  UnderTolerance = 0
  X = -21.8084
  Y = -66.722
FEATURE [TechDraw::DrawViewDimension] Dimension010
  Arbitrary = false
  ArbitraryTolerances = false
  EqualTolerance = true
  FormatSpec = %.2f
  FormatSpecOverTolerance = %+.2f
  FormatSpecUnderTolerance = %+.2f
  Inverted = false
  LockPosition = false
  MeasureType = 1
  OverTolerance = 0
  References2D = -> [ProjItem]
  Rotation = 0
  ScaleType = 0
  TheoreticalExact = false
  Type = 2
  UnderTolerance = 0
  X = 9.28199
  Y = 11.788
FEATURE [TechDraw::DrawViewDimension] Dimension011
  Arbitrary = false
  ArbitraryTolerances = false
  EqualTolerance = true
  FormatSpec = %.2f
  FormatSpecOverTolerance = %+.2f
  FormatSpecUnderTolerance = %+.2f
  Inverted = false
  LockPosition = false
  MeasureType = 1
  OverTolerance = 0
  References2D = -> [ProjItem]
  Rotation = 0
  ScaleType = 0
  TheoreticalExact = false
  Type = 2
  UnderTolerance = 0
  X = 20.2847
  Y = 22.1544
FEATURE [TechDraw::DrawViewDimension] Dimension012
  Arbitrary = false
  ArbitraryTolerances = false
  EqualTolerance = true
  FormatSpec = %.2f
  FormatSpecOverTolerance = %+.2f
  FormatSpecUnderTolerance = %+.2f
  Inverted = false
  LockPosition = false
  MeasureType = 1
  OverTolerance = 0
  References2D = -> [ProjItem]
  Rotation = 0
  ScaleType = 0
  TheoreticalExact = false
  Type = 2
  UnderTolerance = 0
  X = 13.5804
  Y = 51.1966
FEATURE [TechDraw::DrawViewDimension] Dimension013
  Arbitrary = false
  ArbitraryTolerances = false
  EqualTolerance = true
  FormatSpec = %.2f
  FormatSpecOverTolerance = %+.2f
  FormatSpecUnderTolerance = %+.2f
  Inverted = false
  LockPosition = false
  MeasureType = 1
  OverTolerance = 0
  References2D = -> [ProjItem]
  Rotation = 0
  ScaleType = 0
  TheoreticalExact = false
  Type = 2
  UnderTolerance = 0
  X = 13.5804
  Y = 63.2969
FEATURE [TechDraw::DrawViewDimension] Dimension014
  Arbitrary = false
  ArbitraryTolerances = false
  EqualTolerance = true
  FormatSpec = %.2f
  FormatSpecOverTolerance = %+.2f
  FormatSpecUnderTolerance = %+.2f
  Inverted = false
  LockPosition = false
  MeasureType = 1
  OverTolerance = 0
  References2D = -> [ProjItem]
  Rotation = 0
  ScaleType = 0
  TheoreticalExact = false
  Type = 2
  UnderTolerance = 0
  X = 13.5804
  Y = 39.5266
FEATURE [TechDraw::DrawViewDimension] Dimension015
  Arbitrary = false
  ArbitraryTolerances = false
  EqualTolerance = true
  FormatSpec = %.2f
  FormatSpecOverTolerance = %+.2f
  FormatSpecUnderTolerance = %+.2f
  Inverted = false
  LockPosition = false
  MeasureType = 1
  OverTolerance = 0
  References2D = -> [ProjItem]
  Rotation = 0
  ScaleType = 0
  TheoreticalExact = false
  Type = 1
  UnderTolerance = 0
  X = -17.2861
  Y = 66.9147
FEATURE [TechDraw::DrawViewDimension] Dimension016
  Arbitrary = false
  ArbitraryTolerances = false
  EqualTolerance = true
  FormatSpec = %.2f
  FormatSpecOverTolerance = %+.2f
  FormatSpecUnderTolerance = %+.2f
  Inverted = false
  LockPosition = false
  MeasureType = 1
  OverTolerance = 0
  References2D = -> [ProjItem]
  Rotation = 0
  ScaleType = 0
  TheoreticalExact = false
  Type = 2
  UnderTolerance = 0
  X = 20.7713
  Y = 79.0366
FEATURE [TechDraw::DrawViewDimension] Dimension017
  Arbitrary = false
  ArbitraryTolerances = false
  EqualTolerance = true
  FormatSpec = %.2f
  FormatSpecOverTolerance = %+.2f
  FormatSpecUnderTolerance = %+.2f
  Inverted = false
  LockPosition = false
  MeasureType = 1
  OverTolerance = 0
  References2D = -> [ProjItem001]
  Rotation = 0
  ScaleType = 0
  TheoreticalExact = false
  Type = 2
  UnderTolerance = 0
  X = -13.5557
  Y = -1.1404
FEATURE [TechDraw::DrawViewDimension] Dimension018
  Arbitrary = false
  ArbitraryTolerances = false
  EqualTolerance = true
  FormatSpec = %.2f
  FormatSpecOverTolerance = %+.2f
  FormatSpecUnderTolerance = %+.2f
  Inverted = false
  LockPosition = false
  MeasureType = 1
  OverTolerance = 0
  References2D = -> [ProjItem001]
  Rotation = 0
  ScaleType = 0
  TheoreticalExact = false
  Type = 1
  UnderTolerance = 0
  X = -1.0861
  Y = 80.5895
FEATURE [TechDraw::DrawViewDimension] Dimension019
  Arbitrary = false
  ArbitraryTolerances = false
  EqualTolerance = true
  FormatSpec = %.2f
  FormatSpecOverTolerance = %+.2f
  FormatSpecUnderTolerance = %+.2f
  Inverted = false
  LockPosition = false
  MeasureType = 1
  OverTolerance = 0
  References2D = -> [ProjItem002]
  Rotation = 0
  ScaleType = 0
  TheoreticalExact = false
  Type = 1
  UnderTolerance = 0
  X = -0.543049
  Y = 11.8047
FEATURE [TechDraw::DrawViewDimension] Dimension020
  Arbitrary = false
  ArbitraryTolerances = false
  EqualTolerance = true
  FormatSpec = ⌀%.2f
  FormatSpecOverTolerance = %+.2f
  FormatSpecUnderTolerance = %+.2f
  Inverted = false
  LockPosition = false
  MeasureType = 1
  OverTolerance = 0
  References2D = -> [ProjItem]
  Rotation = 0
  ScaleType = 0
  TheoreticalExact = false
  Type = 5
  UnderTolerance = 0
  X = -28.5336
  Y = 41.9241
FEATURE [TechDraw::DrawViewDimension] Dimension021
  Arbitrary = false
  ArbitraryTolerances = false
  EqualTolerance = true
  FormatSpec = ⌀%.2f
  FormatSpecOverTolerance = %+.2f
  FormatSpecUnderTolerance = %+.2f
  Inverted = false
  LockPosition = false
  MeasureType = 1
  OverTolerance = 0
  References2D = -> [ProjItem]
  Rotation = 0
  ScaleType = 0
  TheoreticalExact = false
  Type = 5
  UnderTolerance = 0
  X = -26.8721
  Y = 61.6716
FEATURE [TechDraw::DrawViewDimension] Dimension022
  Arbitrary = false
  ArbitraryTolerances = false
  EqualTolerance = true
  FormatSpec = ⌀%.2f
  FormatSpecOverTolerance = %+.2f
  FormatSpecUnderTolerance = %+.2f
  Inverted = false
  LockPosition = false
  MeasureType = 1
  OverTolerance = 0
  References2D = -> [ProjItem]
  Rotation = 0
  ScaleType = 0
  TheoreticalExact = false
  Type = 5
  UnderTolerance = 0
  X = -33.8173
  Y = -24.6167
FEATURE [TechDraw::DrawViewDimension] Dimension023
  Arbitrary = false
  ArbitraryTolerances = false
  EqualTolerance = true
  FormatSpec = %.2f
  FormatSpecOverTolerance = %+.2f
  FormatSpecUnderTolerance = %+.2f
  Inverted = false
  LockPosition = false
  MeasureType = 1
  OverTolerance = 0
  References2D = -> [ProjItem]
  Rotation = 0
  ScaleType = 0
  TheoreticalExact = false
  Type = 2
  UnderTolerance = 0
  X = 13.8374
  Y = -49.9492
FEATURE [TechDraw::DrawViewDimension] Dimension034
  Arbitrary = true
  ArbitraryTolerances = false
  EqualTolerance = true
  FormatSpec = ⌀M5 c/ rosca
  FormatSpecOverTolerance = %+.2f
  FormatSpecUnderTolerance = %+.2f
  Inverted = false
  LockPosition = false
  MeasureType = 1
  OverTolerance = 0
  References2D = -> [ProjItem]
  Rotation = 0
  ScaleType = 0
  TheoreticalExact = false
  Type = 5
  UnderTolerance = 0
  X = -23.9847
  Y = -59.5306
FEATURE [TechDraw::DrawViewDimension] Dimension036
  Arbitrary = false
  ArbitraryTolerances = false
  EqualTolerance = true
  FormatSpec = ⌀%.2f
  FormatSpecOverTolerance = %+.2f
  FormatSpecUnderTolerance = %+.2f
  Inverted = false
  LockPosition = false
  MeasureType = 1
  OverTolerance = 0
  References2D = -> [ProjItem]
  Rotation = 0
  ScaleType = 0
  TheoreticalExact = false
  Type = 5
  UnderTolerance = 0
  X = -29.5552
  Y = 34.0748
FEATURE [TechDraw::DrawViewDimension] Dimension037
  Arbitrary = false
  ArbitraryTolerances = false
  EqualTolerance = true
  FormatSpec = ⌀%.2f
  FormatSpecOverTolerance = %+.2f
  FormatSpecUnderTolerance = %+.2f
  Inverted = false
  LockPosition = false
  MeasureType = 1
  OverTolerance = 0
  References2D = -> [ProjItem]
  Rotation = 0
  ScaleType = 0
  TheoreticalExact = false
  Type = 5
  UnderTolerance = 0
  X = -24.9027
  Y = -16.2327
FEATURE [TechDraw::DrawViewDimension] Dimension038
  Arbitrary = false
  ArbitraryTolerances = false
  EqualTolerance = true
  FormatSpec = ⌀%.2f
  FormatSpecOverTolerance = %+.2f
  FormatSpecUnderTolerance = %+.2f
  Inverted = false
  LockPosition = false
  MeasureType = 1
  OverTolerance = 0
  References2D = -> [ProjItem]
  Rotation = 0
  ScaleType = 0
  TheoreticalExact = false
  Type = 5
  UnderTolerance = 0
  X = -34.52
  Y = -37.7093
FEATURE [TechDraw::DrawViewDimension] Dimension039
  Arbitrary = false
  ArbitraryTolerances = false
  EqualTolerance = true
  FormatSpec = ⌀%.2f
  FormatSpecOverTolerance = %+.2f
  FormatSpecUnderTolerance = %+.2f
  Inverted = false
  LockPosition = false
  MeasureType = 1
  OverTolerance = 0
  References2D = -> [ProjItem]
  Rotation = 0
  ScaleType = 0
  TheoreticalExact = false
  Type = 5
  UnderTolerance = 0
  X = -27.8953
  Y = 52.4132
FEATURE [TechDraw::DrawViewPart] View
  CoarseView = false
  Direction = (0.577,-0.577,0.577)
  Focus = 100
  HardHidden = false
  IsoCount = 0
  IsoHidden = false
  IsoVisible = false
  LockPosition = false
  Perspective = false
  Rotation = 0
  ScaleType = 0
  SeamHidden = false
  SeamVisible = true
  SmoothHidden = false
  SmoothVisible = true
  Source = -> [Body]
  X = 100.708
  XDirection = (0.707,0.707,0)
  Y = 245.598
FEATURE [PartDesign::CoordinateSystem] LCS_0
  AttacherType = Attacher::AttachEngine3D
  MapMode = 2
  Support = -> [X_Axis002]
FEATURE [Part::FeaturePython] Tube  # WARN: FeaturePython — macro-defined, semantics opaque (R4)
  AttacherType = Attacher::AttachEngine3D
  Height = 2
  InnerRadius = 3
  OuterRadius = 4
FEATURE [Part::FeaturePython] Tube001  # WARN: FeaturePython — macro-defined, semantics opaque (R4)
  AttacherType = Attacher::AttachEngine3D
  Height = 1
  InnerRadius = 1.5
  OuterRadius = 3
FEATURE [Part::MultiFuse] Fusion
  Shapes = -> [Tube,Tube001]
FEATURE [PartDesign::FeatureBase] BaseFeature
  BaseFeature = -> Fusion
FEATURE [PartDesign::Body] insulator
  BaseFeature = -> Fusion
  Group = -> [BaseFeature,LCS_0]
  Origin = -> Origin002
  Placement = pos=(50,0,0) rot=(0,0,1;0rad)
  Tip = -> BaseFeature
FEATURE [TechDraw::DrawViewDimension] Dimension046
  Arbitrary = false
  ArbitraryTolerances = false
  EqualTolerance = true
  FormatSpec = ⌀%.4f
  FormatSpecOverTolerance = %+.4f
  FormatSpecUnderTolerance = %+.4f
  Inverted = false
  LockPosition = false
  MeasureType = 1
  OverTolerance = 0
  References2D = -> [ProjItem003]
  Rotation = 0
  ScaleType = 0
  TheoreticalExact = false
  Type = 5
  UnderTolerance = 0
  X = -25.2801
  Y = -3.641
FEATURE [TechDraw::DrawViewDimension] Dimension047
  Arbitrary = false
  ArbitraryTolerances = false
  EqualTolerance = true
  FormatSpec = %.4f
  FormatSpecOverTolerance = %+.4f
  FormatSpecUnderTolerance = %+.4f
  Inverted = false
  LockPosition = false
  MeasureType = 1
  OverTolerance = 0
  References2D = -> [ProjItem]
  Rotation = 0
  ScaleType = 0
  TheoreticalExact = false
  Type = 0
  UnderTolerance = 0
  X = -16.9882
  Y = 6.72652
FEATURE [TechDraw::DrawPage] Page
  KeepUpdated = true
  NextBalloonIndex = 1
  ProjectionType = 0
  Template = -> Template
  Views = -> [Sheet,ProjGroup,ProjGroup001,Dimension001,Dimension,Dimension003,Dimension004,Dimension005,Dimension006,Dimension007,Dimension008,Dimension009,Dimension010,Dimension011,Dimension012,Dimension013,Dimension014,Dimension015,Dimension016,Dimension017,Dimension018,Dimension019,Dimension020,Dimension021,Dimension022,Dimension023,Dimension024,Dimension025,Dimension026,Dimension027,Dimension028,+18 more]
